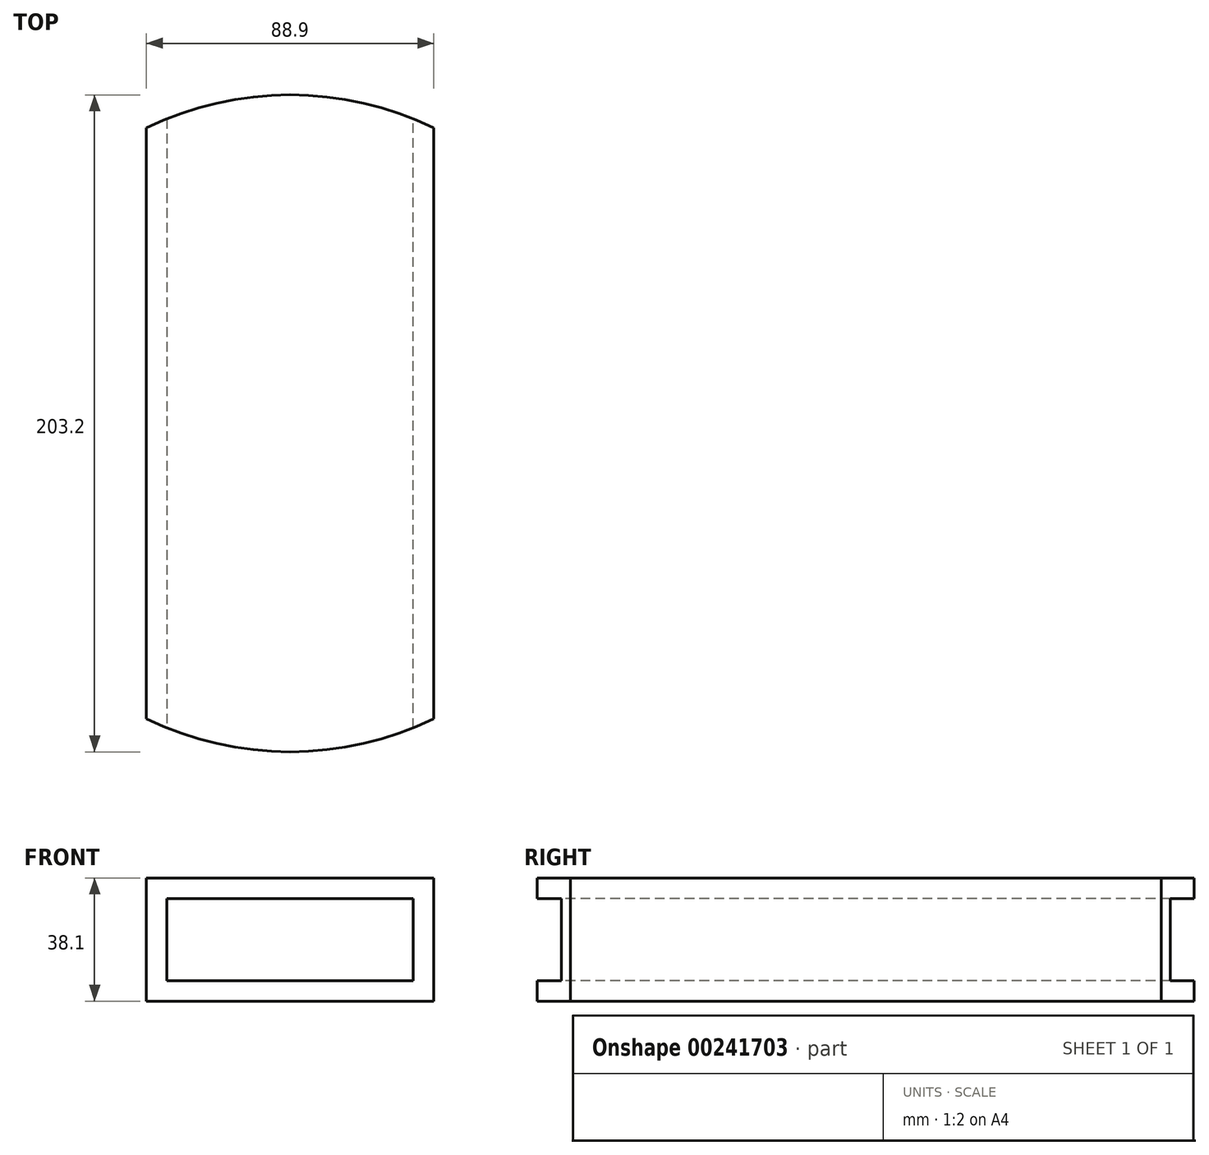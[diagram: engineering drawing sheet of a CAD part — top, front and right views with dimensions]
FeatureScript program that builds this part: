
annotation { "Feature Type Name" : "Feature", "Feature Type Description" : "" }
export const myFeature = defineFeature(function(context is Context, id is Id, definition is map)
    precondition{}
    {
        {
            var Q0;
            Q0=qCreatedBy(makeId("Top.planeOp"),FACE);
            var sketch = newSketch(context, id + "F0", { "sketchPlane" : qUnion([Q0])});
            skPoint(sketch, "E0.middle", {"position": v(0, 0) * mm});
            skArc(sketch, "E1", {"start": v(0, 101.6) * mm, "mid": v(-22.8, 99) * mm, "end": v(-44.45, 91.36) * mm});
            skArc(sketch, "E2", {"start": v(44.45, 91.36) * mm, "mid": v(22.8, 99) * mm, "end": v(0, 101.6) * mm});
            skArc(sketch, "E3", {"start": v(-44.45, -91.36) * mm, "mid": v(-22.8, -99) * mm, "end": v(0, -101.6) * mm});
            skArc(sketch, "E4", {"start": v(0, -101.6) * mm, "mid": v(22.8, -99) * mm, "end": v(44.45, -91.36) * mm});
            skLineSegment(sketch, "E5", {"start": v(-44.45, 91.36) * mm, "end": v(-44.45, -91.36) * mm});
            skLineSegment(sketch, "E6", {"start": v(44.45, -91.36) * mm, "end": v(44.45, 91.36) * mm});
            skSolve(sketch);
        }
        {
            var Q0;
            Q0=makeQuery(id+"F0.imprint","IMPRINT",FACE,{"disambiguationData":[TD([[makeQuery(id+"F0.imprint","IMPRINT",EDGE,{"derivedFrom":sQuery(id+"F0.wireOp",EDGE,"E1")}),1.0]])]});
            extrude(context, id + "F1", {"entities" : qUnion([Q0]), "depth" : 38.1 * mm});
        }
        {
            var Q0;
            Q0=makeQuery(id+"F1.opExtrude","SWEPT_FACE",FACE,{"disambiguationData":[OSD([sQuery(id+"F0.wireOp",EDGE,"E3"),sQuery(id+"F0.wireOp",EDGE,"E4")])]});
            var Q1;
            Q1=makeQuery(id+"F1.opExtrude","SWEPT_FACE",FACE,{"disambiguationData":[OSD([sQuery(id+"F0.wireOp",EDGE,"E1"),sQuery(id+"F0.wireOp",EDGE,"E2")])]});
            shell(context, id + "F2", {"entities" : qUnion([Q0, Q1]), "thickness" : 6.35 * mm});
        }
    });
